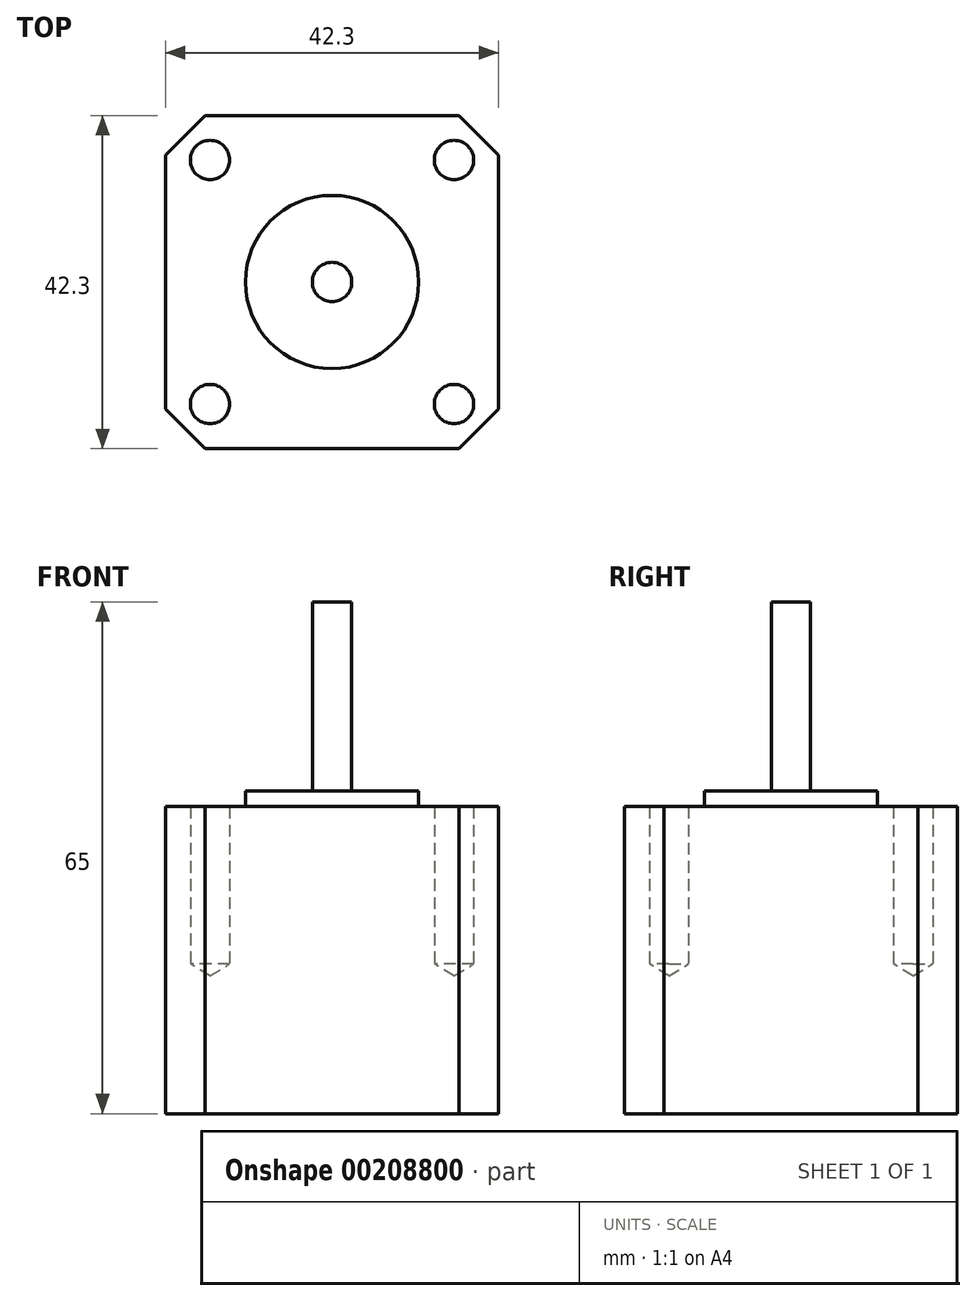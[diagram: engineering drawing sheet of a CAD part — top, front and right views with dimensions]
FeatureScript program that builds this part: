
annotation { "Feature Type Name" : "Feature", "Feature Type Description" : "" }
export const myFeature = defineFeature(function(context is Context, id is Id, definition is map)
    precondition{}
    {
        {
            var Q0;
            Q0=qCreatedBy(makeId("Top.planeOp"),FACE);
            var sketch = newSketch(context, id + "F0", { "sketchPlane" : qUnion([Q0])});
            skLineSegment(sketch, "E0.bottom", {"start": v(0, 42.3) * mm, "end": v(42.3, 42.3) * mm});
            skLineSegment(sketch, "E0.top", {"start": v(0, 0) * mm, "end": v(42.3, 0) * mm});
            skLineSegment(sketch, "E0.left", {"start": v(0, 42.3) * mm, "end": v(0, 0) * mm});
            skLineSegment(sketch, "E0.right", {"start": v(42.3, 42.3) * mm, "end": v(42.3, 0) * mm});
            skSolve(sketch);
        }
        {
            var Q0;
            Q0=qSketchRegion(id+"F0",true);
            extrude(context, id + "F1", {"entities" : qUnion([Q0]), "depth" : 39 * mm});
        }
        {
            var Q0;
            Q0=makeQuery(id+"F1.opExtrude","CAP_FACE",FACE,{"disambiguationData":[OSD([sQuery(id+"F0.wireOp",EDGE,"E0.bottom"),sQuery(id+"F0.wireOp",EDGE,"E0.top"),sQuery(id+"F0.wireOp",EDGE,"E0.left"),sQuery(id+"F0.wireOp",EDGE,"E0.right")])],"isStart":false});
            var sketch = newSketch(context, id + "F2", { "sketchPlane" : qUnion([Q0])});
            skCircle(sketch, "E1", {"center": v(21.15, 21.15) * mm, "radius": 11 * mm});
            skSolve(sketch);
        }
        {
            var Q0;
            Q0=qSketchRegion(id+"F2",true);
            extrude(context, id + "F3", {"entities" : qUnion([Q0]), "operationType" : NewBodyOperationType.ADD, "depth" : 2 * mm});
        }
        {
            var Q0;
            Q0=makeQuery(id+"F3.opExtrude","CAP_FACE",FACE,{"disambiguationData":[OSD([sQuery(id+"F2.wireOp",EDGE,"E1")])],"isStart":false});
            var sketch = newSketch(context, id + "F4", { "sketchPlane" : qUnion([Q0])});
            skCircle(sketch, "E2", {"center": v(21.15, 21.15) * mm, "radius": 2.5 * mm});
            skSolve(sketch);
        }
        {
            var Q0;
            Q0=qSketchRegion(id+"F4",true);
            extrude(context, id + "F5", {"entities" : qUnion([Q0]), "depth" : 24 * mm});
        }
        {
            var Q0;
            Q0=makeQuery(id+"F1.opExtrude","CAP_FACE",FACE,{"disambiguationData":[OSD([sQuery(id+"F0.wireOp",EDGE,"E0.bottom"),sQuery(id+"F0.wireOp",EDGE,"E0.top"),sQuery(id+"F0.wireOp",EDGE,"E0.left"),sQuery(id+"F0.wireOp",EDGE,"E0.right")])],"isStart":false});
            var sketch = newSketch(context, id + "F6", { "sketchPlane" : qUnion([Q0])});
            skPoint(sketch, "E3", {"position": v(5.65, 36.65) * mm});
            skPoint(sketch, "E4", {"position": v(36.65, 36.65) * mm});
            skPoint(sketch, "E5", {"position": v(36.65, 5.65) * mm});
            skPoint(sketch, "E6", {"position": v(5.65, 5.65) * mm});
            skSolve(sketch);
        }
        {
            var Q0;
            Q0=sQuery(id+"F6.wireOp",VERTEX,"E3");
            var Q1;
            Q1=sQuery(id+"F6.wireOp",VERTEX,"E4");
            var Q2;
            Q2=sQuery(id+"F6.wireOp",VERTEX,"E5");
            var Q3;
            Q3=sQuery(id+"F6.wireOp",VERTEX,"E6");
            var Q4;
            Q4=makeQuery(id+"F1.opExtrude","SWEPT_BODY",BODY,{"disambiguationData":[OSD([sQuery(id+"F0.wireOp",EDGE,"E0.bottom"),sQuery(id+"F0.wireOp",EDGE,"E0.top"),sQuery(id+"F0.wireOp",EDGE,"E0.left"),sQuery(id+"F0.wireOp",EDGE,"E0.right")])]});
            hole(context, id + "F7", {"style" : HoleStyle.SIMPLE, "holeDiameter" : 5 * mm, "endStyle" : HoleEndStyle.BLIND, "holeDepth" : 20 * mm, "locations" : qUnion([Q0, Q1, Q2, Q3]), "scope" : qUnion([Q4])});
        }
        {
            var Q0;
            Q0=makeQuery(id+"F1.opExtrude","SWEPT_EDGE",EDGE,{"disambiguationData":[OSD([sQuery(id+"F0.wireOp",EDGE,"E0.bottom"),sQuery(id+"F0.wireOp",EDGE,"E0.left")])]});
            var Q1;
            Q1=makeQuery(id+"F1.opExtrude","SWEPT_EDGE",EDGE,{"disambiguationData":[OSD([sQuery(id+"F0.wireOp",EDGE,"E0.top"),sQuery(id+"F0.wireOp",EDGE,"E0.left")])]});
            var Q2;
            Q2=makeQuery(id+"F1.opExtrude","SWEPT_EDGE",EDGE,{"disambiguationData":[OSD([sQuery(id+"F0.wireOp",EDGE,"E0.top"),sQuery(id+"F0.wireOp",EDGE,"E0.right")])]});
            var Q3;
            Q3=makeQuery(id+"F1.opExtrude","SWEPT_EDGE",EDGE,{"disambiguationData":[OSD([sQuery(id+"F0.wireOp",EDGE,"E0.bottom"),sQuery(id+"F0.wireOp",EDGE,"E0.right")])]});
            chamfer(context, id + "F8", {"entities" : qUnion([Q0, Q1, Q2, Q3]), "width" : 5 * mm, "tangentPropagation" : true});
        }
    });
